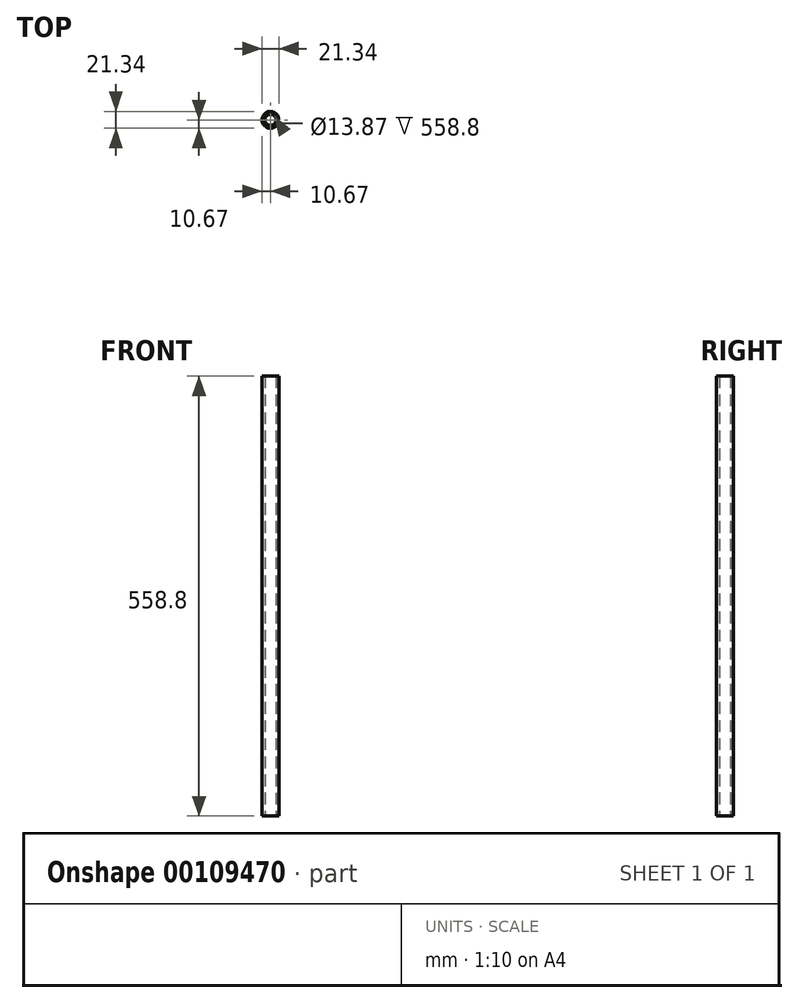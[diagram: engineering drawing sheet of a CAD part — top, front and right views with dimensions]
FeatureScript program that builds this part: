
annotation { "Feature Type Name" : "Feature", "Feature Type Description" : "" }
export const myFeature = defineFeature(function(context is Context, id is Id, definition is map)
    precondition{}
    {
        {
            var Q0;
            Q0=qCreatedBy(makeId("Top.planeOp"),FACE);
            var sketch = newSketch(context, id + "F0", { "sketchPlane" : qUnion([Q0])});
            skCircle(sketch, "E0", {"center": v(0, 0) * mm, "radius": 10.67 * mm});
            skCircle(sketch, "E1", {"center": v(0, 0) * mm, "radius": 6.93 * mm});
            skSolve(sketch);
        }
        {
            var Q0;
            Q0=makeQuery(id+"F0.imprint","IMPRINT",FACE,{"disambiguationData":[TD([[makeQuery(id+"F0.imprint","IMPRINT",EDGE,{"derivedFrom":sQuery(id+"F0.wireOp",EDGE,"E0")}),1.0]])]});
            extrude(context, id + "F1", {"entities" : qUnion([Q0]), "depth" : 558.8 * mm});
        }
    });
